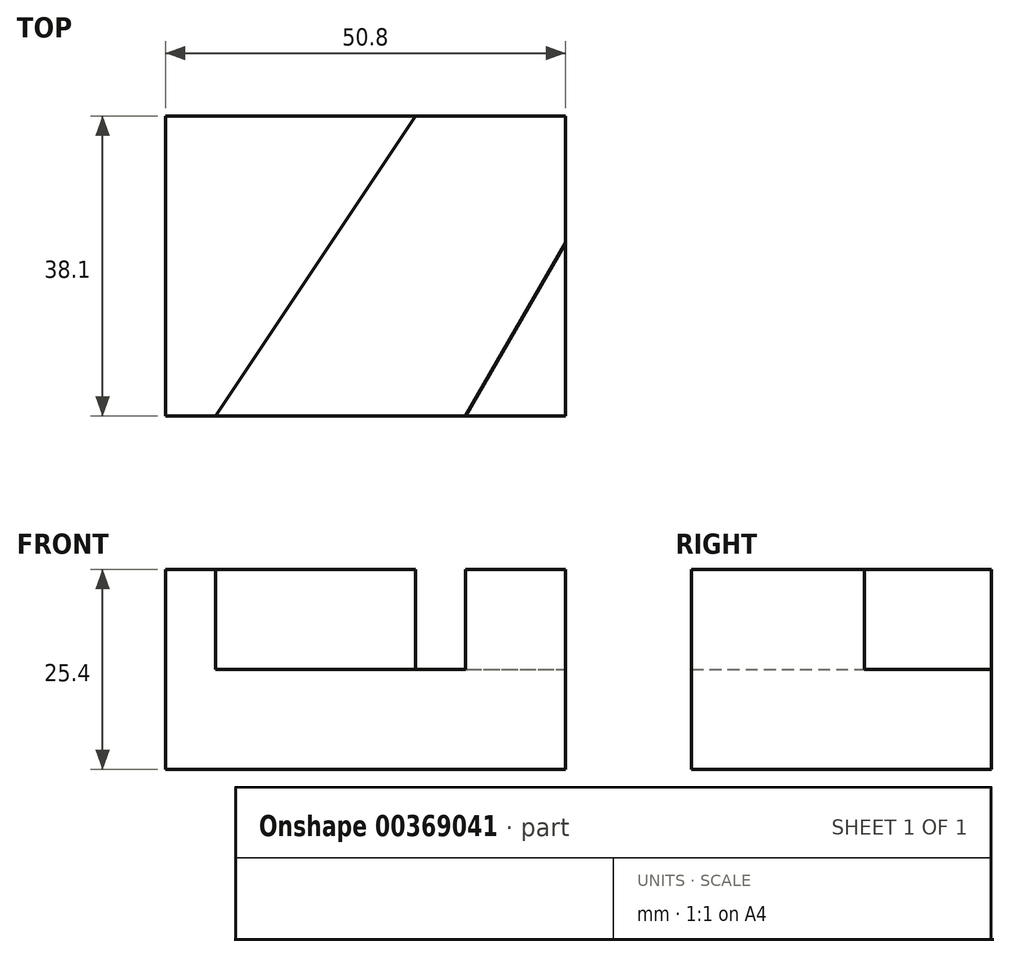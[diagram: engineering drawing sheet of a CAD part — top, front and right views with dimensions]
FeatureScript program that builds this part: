
annotation { "Feature Type Name" : "Feature", "Feature Type Description" : "" }
export const myFeature = defineFeature(function(context is Context, id is Id, definition is map)
    precondition{}
    {
        {
            var Q0;
            Q0=qCreatedBy(makeId("Front.planeOp"),FACE);
            var sketch = newSketch(context, id + "F0", { "sketchPlane" : qUnion([Q0])});
            skLineSegment(sketch, "E0", {"start": v(0, 0) * mm, "end": v(0, 25.4) * mm});
            skLineSegment(sketch, "E1", {"start": v(0, 25.4) * mm, "end": v(50.8, 25.4) * mm});
            skLineSegment(sketch, "E2", {"start": v(50.8, 25.4) * mm, "end": v(50.8, 0) * mm});
            skLineSegment(sketch, "E3", {"start": v(50.8, 0) * mm, "end": v(0, 0) * mm});
            skSolve(sketch);
        }
        {
            var Q0;
            Q0=makeQuery(id+"F0.imprint","IMPRINT",FACE,{"disambiguationData":[TD([[makeQuery(id+"F0.imprint","IMPRINT",EDGE,{"derivedFrom":sQuery(id+"F0.wireOp",EDGE,"E0")}),-1.0]])]});
            extrude(context, id + "F1", {"entities" : qUnion([Q0]), "depth" : 38.1 * mm});
        }
        {
            var Q0;
            Q0=makeQuery(id+"F1.opExtrude","CAP_FACE",FACE,{"disambiguationData":[OSD([sQuery(id+"F0.wireOp",EDGE,"E0"),sQuery(id+"F0.wireOp",EDGE,"E1"),sQuery(id+"F0.wireOp",EDGE,"E2"),sQuery(id+"F0.wireOp",EDGE,"E3")])],"isStart":false});
            var sketch = newSketch(context, id + "F2", { "sketchPlane" : qUnion([Q0])});
            skLineSegment(sketch, "E4", {"start": v(6.35, 25.4) * mm, "end": v(6.35, 12.7) * mm});
            skLineSegment(sketch, "E5", {"start": v(6.35, 12.7) * mm, "end": v(38.1, 12.7) * mm});
            skLineSegment(sketch, "E6", {"start": v(38.1, 12.7) * mm, "end": v(38.1, 25.4) * mm});
            skLineSegment(sketch, "E7", {"start": v(38.1, 25.4) * mm, "end": v(6.35, 25.4) * mm});
            skSolve(sketch);
        }
        {
            var Q0;
            Q0=makeQuery(id+"F2.imprint","IMPRINT",FACE,{"disambiguationData":[TD([[makeQuery(id+"F2.imprint","IMPRINT",EDGE,{"derivedFrom":sQuery(id+"F2.wireOp",EDGE,"E4")}),1.0]])]});
            extrude(context, id + "F3", {"entities" : qUnion([Q0]), "operationType" : NewBodyOperationType.REMOVE, "oppositeDirection" : true, "depth" : 38.1 * mm});
        }
        {
            var Q0;
            Q0=makeQuery(id+"F3.boolean.opBoolean","COPY",FACE,{"derivedFrom":makeQuery(id+"F3.opExtrude","SWEPT_FACE",FACE,{"disambiguationData":[OSD([sQuery(id+"F2.wireOp",EDGE,"E5")])]})});
            var sketch = newSketch(context, id + "F4", { "sketchPlane" : qUnion([Q0])});
            skLineSegment(sketch, "E8", {"start": v(6.35, -38.1) * mm, "end": v(31.75, 0) * mm});
            skSolve(sketch);
        }
        {
            var Q0;
            {var subQ0=sQuery(id+"F4.wireOp",EDGE,"E8");Q0=makeQuery(id+"F4.imprint","IMPRINT",FACE,{"disambiguationData":[TD([[makeQuery(id+"F4.imprint","IMPRINT",EDGE,{"derivedFrom":subQ0}),1.0]])]});}
            extrude(context, id + "F5", {"entities" : qUnion([Q0]), "operationType" : NewBodyOperationType.ADD, "depth" : 12.7 * mm});
        }
        {
            var Q0;
            {var subQ1=sQuery(id+"F0.wireOp",EDGE,"E2");var subQ2=sQuery(id+"F0.wireOp",EDGE,"E1");Q0=makeQuery(id+"F3.boolean.opBoolean","SPLIT",FACE,{"disambiguationData":[TD([makeQuery(id+"F1.opExtrude","SWEPT_FACE",FACE,{"disambiguationData":[OSD([subQ1])]})])],"derivedFrom":makeQuery(id+"F1.opExtrude","SWEPT_FACE",FACE,{"disambiguationData":[OSD([subQ2])]})});}
            var sketch = newSketch(context, id + "F6", { "sketchPlane" : qUnion([Q0])});
            skLineSegment(sketch, "E9", {"start": v(38.1, -38.1) * mm, "end": v(50.8, -16.1) * mm});
            skSolve(sketch);
        }
        {
            var Q0;
            {var subQ0=sQuery(id+"F6.wireOp",EDGE,"E9");Q0=makeQuery(id+"F6.imprint","IMPRINT",FACE,{"disambiguationData":[TD([[makeQuery(id+"F6.imprint","IMPRINT",EDGE,{"derivedFrom":subQ0}),1.0]])]});}
            extrude(context, id + "F7", {"entities" : qUnion([Q0]), "operationType" : NewBodyOperationType.REMOVE, "oppositeDirection" : true, "depth" : 12.7 * mm});
        }
    });
